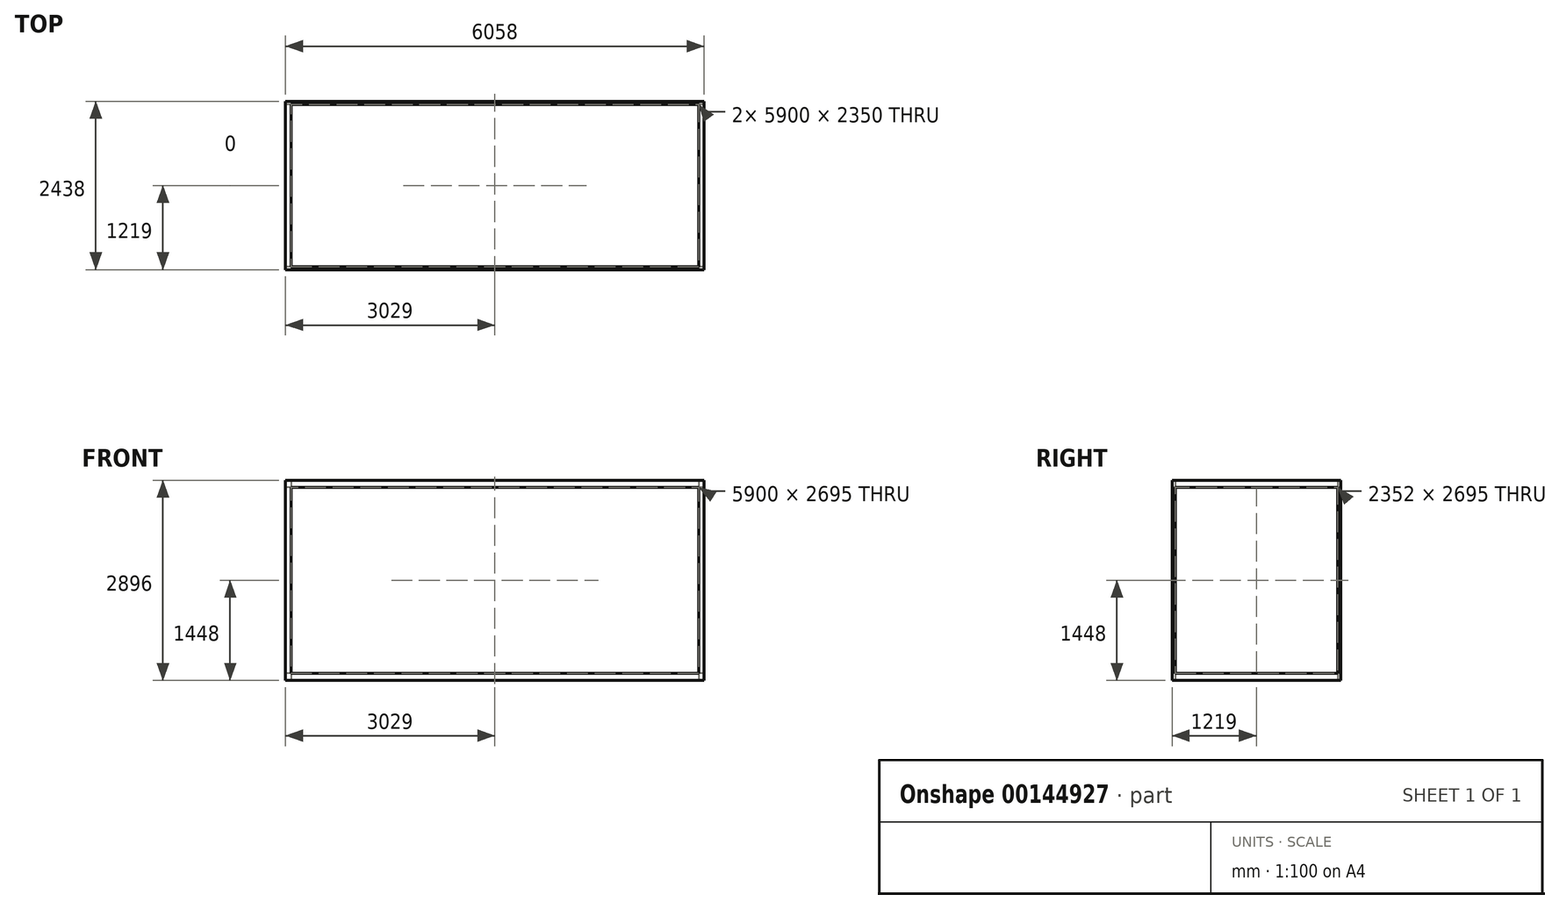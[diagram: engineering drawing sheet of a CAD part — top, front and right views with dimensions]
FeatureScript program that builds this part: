
annotation { "Feature Type Name" : "Feature", "Feature Type Description" : "" }
export const myFeature = defineFeature(function(context is Context, id is Id, definition is map)
    precondition{}
    {
        {
            var Q0;
            Q0=qCreatedBy(makeId("Top.planeOp"),FACE);
            var sketch = newSketch(context, id + "F4", { "sketchPlane" : qUnion([Q0])});
            skLineSegment(sketch, "E0.bottom", {"start": v(2950, -1175) * mm, "end": v(-2950, -1175) * mm});
            skLineSegment(sketch, "E0.top", {"start": v(2950, 1175) * mm, "end": v(-2950, 1175) * mm});
            skLineSegment(sketch, "E0.left", {"start": v(2950, -1175) * mm, "end": v(2950, 1175) * mm});
            skLineSegment(sketch, "E0.right", {"start": v(-2950, -1175) * mm, "end": v(-2950, 1175) * mm});
            skPoint(sketch, "E0.middle", {"position": v(0, 0) * mm});
            skLineSegment(sketch, "E1.bottom", {"start": v(3029, -1219) * mm, "end": v(-3029, -1219) * mm});
            skLineSegment(sketch, "E1.top", {"start": v(3029, 1219) * mm, "end": v(-3029, 1219) * mm});
            skLineSegment(sketch, "E1.left", {"start": v(3029, -1219) * mm, "end": v(3029, 1219) * mm});
            skLineSegment(sketch, "E1.right", {"start": v(-3029, -1219) * mm, "end": v(-3029, 1219) * mm});
            skSolve(sketch);
        }
        {
            var Q0;
            Q0=qSketchRegion(id+"F4",true);
            extrude(context, id + "F0", {"entities" : qUnion([Q0]), "depth" : 2896 * mm});
        }
        {
            var Q0;
            Q0=makeQuery(id+"F0.opExtrude","SWEPT_FACE",FACE,{"disambiguationData":[OSD([sQuery(id+"F4.wireOp",EDGE,"E1.bottom")])]});
            var sketch = newSketch(context, id + "F1", { "sketchPlane" : qUnion([Q0])});
            skLineSegment(sketch, "E2.bottom", {"start": v(2950, 100.5) * mm, "end": v(-2950, 100.5) * mm});
            skLineSegment(sketch, "E2.top", {"start": v(2950, 2795.5) * mm, "end": v(-2950, 2795.5) * mm});
            skLineSegment(sketch, "E2.left", {"start": v(2950, 100.5) * mm, "end": v(2950, 2795.5) * mm});
            skLineSegment(sketch, "E2.right", {"start": v(-2950, 100.5) * mm, "end": v(-2950, 2795.5) * mm});
            skPoint(sketch, "E2.middle", {"position": v(0, 1448) * mm});
            skSolve(sketch);
        }
        {
            var Q0;
            Q0=makeQuery(id+"F1.imprint","IMPRINT",FACE,{"disambiguationData":[TD([[makeQuery(id+"F1.imprint","IMPRINT",EDGE,{"derivedFrom":sQuery(id+"F1.wireOp",EDGE,"E2.bottom")}),-1.0]])]});
            extrude(context, id + "F5", {"entities" : qUnion([Q0]), "operationType" : NewBodyOperationType.REMOVE, "endBound" : BoundingType.THROUGH_ALL, "oppositeDirection" : true, "depth" : 25 * mm});
        }
        {
            var Q0;
            Q0=makeQuery(id+"F0.opExtrude","SWEPT_FACE",FACE,{"disambiguationData":[OSD([sQuery(id+"F4.wireOp",EDGE,"E1.right")])]});
            var sketch = newSketch(context, id + "F2", { "sketchPlane" : qUnion([Q0])});
            skLineSegment(sketch, "E3.bottom", {"start": v(1176, 100.5) * mm, "end": v(-1176, 100.5) * mm});
            skLineSegment(sketch, "E3.top", {"start": v(1176, 2795.5) * mm, "end": v(-1176, 2795.5) * mm});
            skLineSegment(sketch, "E3.left", {"start": v(1176, 100.5) * mm, "end": v(1176, 2795.5) * mm});
            skLineSegment(sketch, "E3.right", {"start": v(-1176, 100.5) * mm, "end": v(-1176, 2795.5) * mm});
            skPoint(sketch, "E3.middle", {"position": v(0, 1448) * mm});
            skSolve(sketch);
        }
        {
            var Q0;
            Q0=makeQuery(id+"F2.imprint","IMPRINT",FACE,{"disambiguationData":[TD([[makeQuery(id+"F2.imprint","IMPRINT",EDGE,{"derivedFrom":sQuery(id+"F2.wireOp",EDGE,"E3.bottom")}),-1.0]])]});
            extrude(context, id + "F3", {"entities" : qUnion([Q0]), "operationType" : NewBodyOperationType.REMOVE, "endBound" : BoundingType.THROUGH_ALL, "oppositeDirection" : true, "depth" : 25 * mm});
        }
    });
